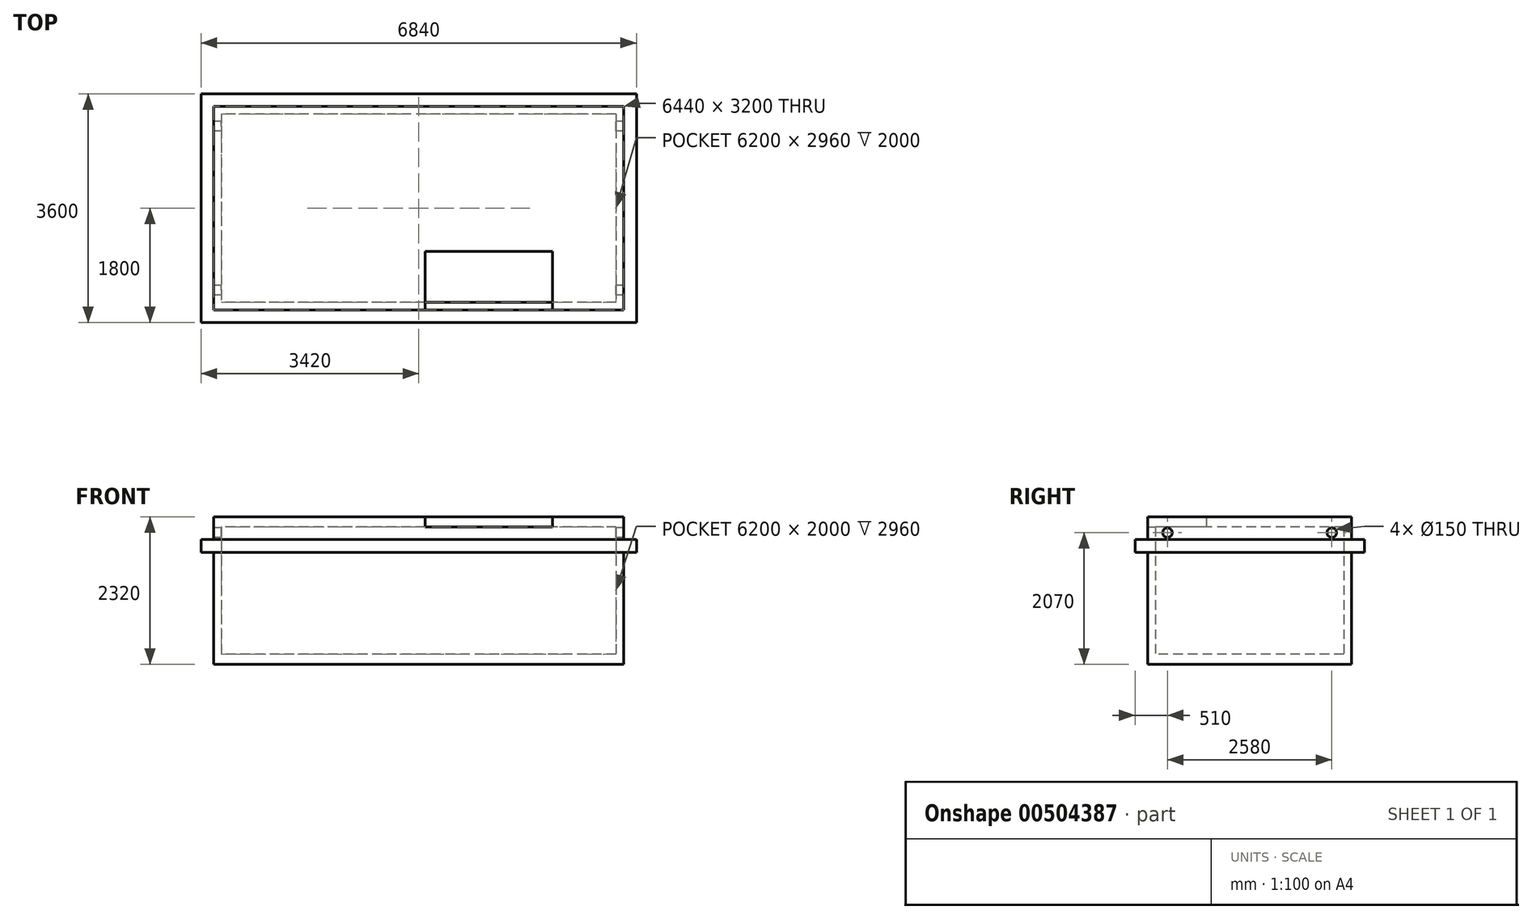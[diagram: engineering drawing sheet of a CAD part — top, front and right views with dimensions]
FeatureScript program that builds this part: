
annotation { "Feature Type Name" : "Feature", "Feature Type Description" : "" }
export const myFeature = defineFeature(function(context is Context, id is Id, definition is map)
    precondition{}
    {
        {
            var Q0;
            Q0=qCreatedBy(makeId("Top.planeOp"),FACE);
            var sketch = newSketch(context, id + "F0", { "sketchPlane" : qUnion([Q0])});
            skLineSegment(sketch, "E0.bottom", {"start": v(3220, 1600) * mm, "end": v(-3220, 1600) * mm});
            skLineSegment(sketch, "E0.top", {"start": v(3220, -1600) * mm, "end": v(-3220, -1600) * mm});
            skLineSegment(sketch, "E0.left", {"start": v(3220, 1600) * mm, "end": v(3220, -1600) * mm});
            skLineSegment(sketch, "E0.right", {"start": v(-3220, 1600) * mm, "end": v(-3220, -1600) * mm});
            skPoint(sketch, "E0.middle", {"position": v(0, 0) * mm});
            skSolve(sketch);
        }
        {
            var Q0;
            Q0=qSketchRegion(id+"F0",true);
            extrude(context, id + "F1", {"entities" : qUnion([Q0]), "depth" : 160 * mm});
        }
        {
            var Q0;
            Q0=makeQuery(id+"F1.opExtrude","CAP_FACE",FACE,{"disambiguationData":[OSD([sQuery(id+"F0.wireOp",EDGE,"E0.bottom"),sQuery(id+"F0.wireOp",EDGE,"E0.top"),sQuery(id+"F0.wireOp",EDGE,"E0.left"),sQuery(id+"F0.wireOp",EDGE,"E0.right")])],"isStart":false});
            var sketch = newSketch(context, id + "F2", { "sketchPlane" : qUnion([Q0])});
            skLineSegment(sketch, "E1.bottom", {"start": v(3100, 1480) * mm, "end": v(-3100, 1480) * mm});
            skLineSegment(sketch, "E1.top", {"start": v(3100, -1480) * mm, "end": v(-3100, -1480) * mm});
            skLineSegment(sketch, "E1.left", {"start": v(3100, 1480) * mm, "end": v(3100, -1480) * mm});
            skLineSegment(sketch, "E1.right", {"start": v(-3100, 1480) * mm, "end": v(-3100, -1480) * mm});
            skPoint(sketch, "E1.middle", {"position": v(0, 0) * mm});
            skLineSegment(sketch, "E2.bottom", {"start": v(3220, 1600) * mm, "end": v(-3220, 1600) * mm});
            skLineSegment(sketch, "E2.top", {"start": v(3220, -1600) * mm, "end": v(-3220, -1600) * mm});
            skLineSegment(sketch, "E2.left", {"start": v(3220, 1600) * mm, "end": v(3220, -1600) * mm});
            skLineSegment(sketch, "E2.right", {"start": v(-3220, 1600) * mm, "end": v(-3220, -1600) * mm});
            skSolve(sketch);
        }
        {
            var Q0;
            Q0=qSketchRegion(id+"F2",true);
            extrude(context, id + "F3", {"entities" : qUnion([Q0]), "operationType" : NewBodyOperationType.ADD, "depth" : 2000 * mm});
        }
        {
            var Q0;
            Q0=makeQuery(id+"F3.opExtrude","CAP_FACE",FACE,{"disambiguationData":[OSD([sQuery(id+"F2.wireOp",EDGE,"E1.bottom"),sQuery(id+"F2.wireOp",EDGE,"E1.top"),sQuery(id+"F2.wireOp",EDGE,"E1.left"),sQuery(id+"F2.wireOp",EDGE,"E1.right"),sQuery(id+"F2.wireOp",EDGE,"E2.bottom"),sQuery(id+"F2.wireOp",EDGE,"E2.top"),sQuery(id+"F2.wireOp",EDGE,"E2.left"),sQuery(id+"F2.wireOp",EDGE,"E2.right")])],"isStart":false});
            var sketch = newSketch(context, id + "F4", { "sketchPlane" : qUnion([Q0])});
            skLineSegment(sketch, "E3", {"start": v(100, -1600) * mm, "end": v(100, -680) * mm});
            skLineSegment(sketch, "E4", {"start": v(100, -680) * mm, "end": v(2100, -680) * mm});
            skLineSegment(sketch, "E5", {"start": v(3220, -1600) * mm, "end": v(3220, 1600) * mm});
            skLineSegment(sketch, "E6", {"start": v(3220, 1600) * mm, "end": v(-3220, 1600) * mm});
            skLineSegment(sketch, "E7", {"start": v(-3220, 1600) * mm, "end": v(-3220, -1600) * mm});
            skLineSegment(sketch, "E8", {"start": v(-3220, -1600) * mm, "end": v(100, -1600) * mm});
            skLineSegment(sketch, "E9", {"start": v(2100, -680) * mm, "end": v(2100, -1600) * mm});
            skLineSegment(sketch, "E10", {"start": v(2100, -1600) * mm, "end": v(3220, -1600) * mm});
            skSolve(sketch);
        }
        {
            var Q0;
            Q0=qSketchRegion(id+"F4",true);
            extrude(context, id + "F5", {"entities" : qUnion([Q0]), "operationType" : NewBodyOperationType.ADD, "depth" : 160 * mm});
        }
        {
            var Q0;
            Q0=makeQuery(id+"F5.boolean.opBoolean","MERGE",FACE,{"derivedFrom":[makeQuery(id+"F3.opExtrude","SWEPT_FACE",FACE,{"disambiguationData":[OSD([sQuery(id+"F2.wireOp",EDGE,"E2.right")])]}),makeQuery(id+"F5.opExtrude","SWEPT_FACE",FACE,{"disambiguationData":[OSD([sQuery(id+"F4.wireOp",EDGE,"E7")])]})]});
            var sketch = newSketch(context, id + "F6", { "sketchPlane" : qUnion([Q0])});
            skCircle(sketch, "E11", {"center": v(-1290, 2070) * mm, "radius": 75 * mm});
            skCircle(sketch, "E12", {"center": v(1290, 2070) * mm, "radius": 75 * mm});
            skSolve(sketch);
        }
        {
            var Q0;
            Q0=qSketchRegion(id+"F6",true);
            extrude(context, id + "F7", {"entities" : qUnion([Q0]), "operationType" : NewBodyOperationType.REMOVE, "endBound" : BoundingType.THROUGH_ALL, "oppositeDirection" : true, "depth" : 25 * mm});
        }
        {
            var Q0;
            {var subQ0=sQuery(id+"F4.wireOp",EDGE,"E4");Q0=makeQuery(id+"F4.imprint","IMPRINT",FACE,{"disambiguationData":[TD([[makeQuery(id+"F4.imprint","IMPRINT",EDGE,{"derivedFrom":subQ0}),-1.0]])]});}
            cPlane(context, id + "F8", {"entities" : qUnion([Q0]), "cplaneType" : CPlaneType.OFFSET, "offset" : 200 * mm, "oppositeDirection" : true, "width" : 150 * mm, "height" : 150 * mm});
        }
        {
            var Q0;
            Q0=qCreatedBy(id+"F8.planeOp",FACE);
            var sketch = newSketch(context, id + "F9", { "sketchPlane" : qUnion([Q0])});
            skLineSegment(sketch, "E13.bottom", {"start": v(-3220, -1600) * mm, "end": v(3220, -1600) * mm});
            skLineSegment(sketch, "E13.top", {"start": v(-3220, 1600) * mm, "end": v(3220, 1600) * mm});
            skLineSegment(sketch, "E13.left", {"start": v(-3220, -1600) * mm, "end": v(-3220, 1600) * mm});
            skLineSegment(sketch, "E13.right", {"start": v(3220, -1600) * mm, "end": v(3220, 1600) * mm});
            skLineSegment(sketch, "E14.0", {"start": v(-3420, -1800) * mm, "end": v(-3420, 1800) * mm});
            skLineSegment(sketch, "E14.1", {"start": v(-3420, -1800) * mm, "end": v(3420, -1800) * mm});
            skLineSegment(sketch, "E14.2", {"start": v(3420, -1800) * mm, "end": v(3420, 1800) * mm});
            skLineSegment(sketch, "E14.3", {"start": v(-3420, 1800) * mm, "end": v(3420, 1800) * mm});
            skSolve(sketch);
        }
        {
            var Q0;
            Q0 = qSketchRegion(id + "F9", true);
            extrude(context, id + "F10", {"entities" : qUnion([Q0]), "operationType" : NewBodyOperationType.ADD, "oppositeDirection" : true, "depth" : 200 * mm});
        }
    });
